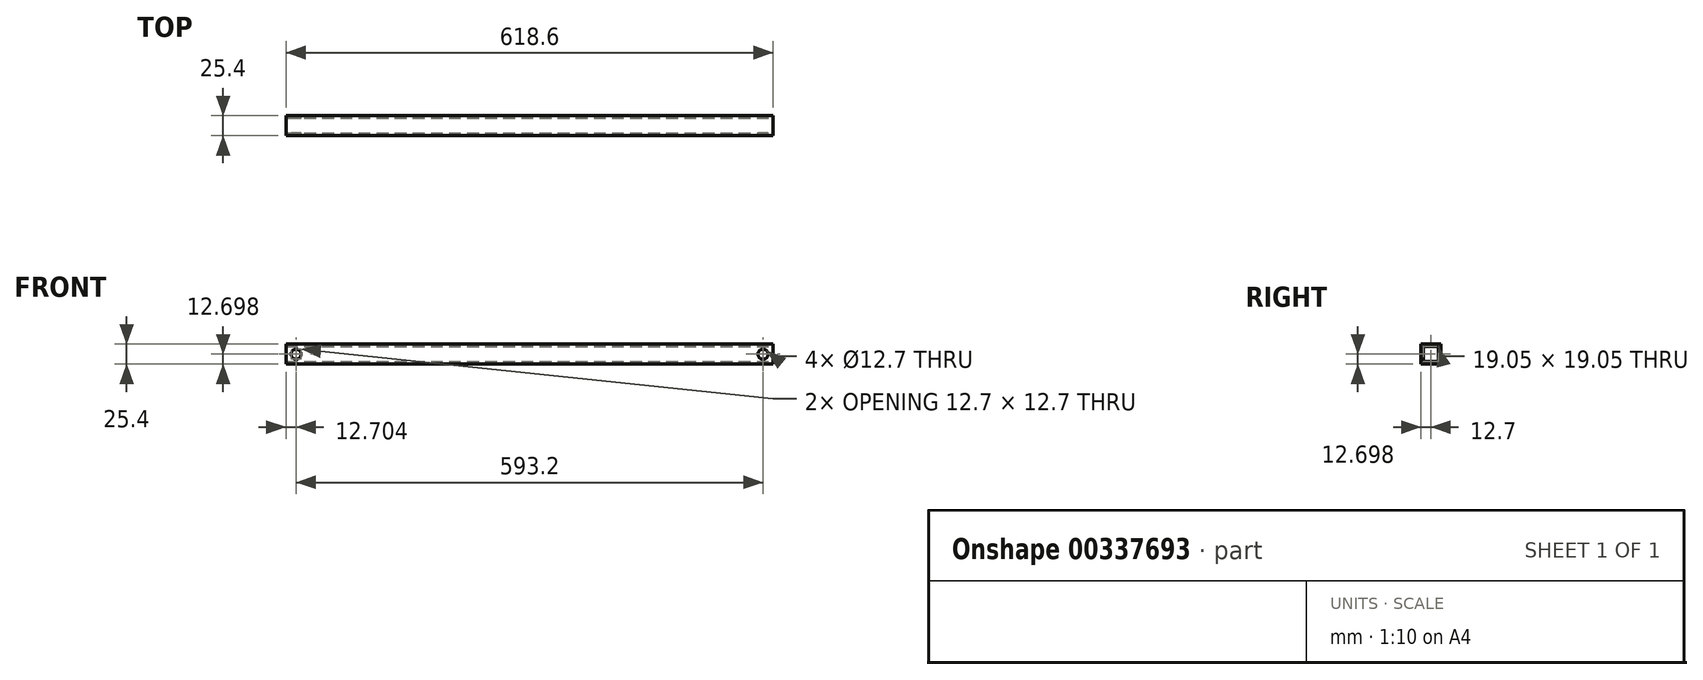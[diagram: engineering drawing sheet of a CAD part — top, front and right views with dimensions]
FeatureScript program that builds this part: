
annotation { "Feature Type Name" : "Feature", "Feature Type Description" : "" }
export const myFeature = defineFeature(function(context is Context, id is Id, definition is map)
    precondition{}
    {
        {
            var Q0;
            Q0=qCreatedBy(makeId("Front.planeOp"),FACE);
            var sketch = newSketch(context, id + "F0", { "sketchPlane" : qUnion([Q0])});
            skLineSegment(sketch, "E0.bottom", {"start": v(-291.49, -54.8) * mm, "end": v(301.71, -54.8) * mm});
            skLineSegment(sketch, "E0.top", {"start": v(-291.49, -80.2) * mm, "end": v(301.71, -80.2) * mm});
            skCircle(sketch, "E1", {"center": v(-291.49, -67.5) * mm, "radius": 6.35 * mm});
            skCircle(sketch, "E2", {"center": v(301.71, -67.5) * mm, "radius": 6.35 * mm});
            skLineSegment(sketch, "E3.bottom", {"start": v(-291.49, -54.8) * mm, "end": v(-304.19, -54.8) * mm});
            skLineSegment(sketch, "E3.top", {"start": v(-291.49, -80.2) * mm, "end": v(-304.19, -80.2) * mm});
            skLineSegment(sketch, "E3.right", {"start": v(-304.19, -54.8) * mm, "end": v(-304.19, -80.2) * mm});
            skLineSegment(sketch, "E4.bottom", {"start": v(301.71, -80.2) * mm, "end": v(314.41, -80.2) * mm});
            skLineSegment(sketch, "E4.top", {"start": v(301.71, -54.8) * mm, "end": v(314.41, -54.8) * mm});
            skLineSegment(sketch, "E4.right", {"start": v(314.41, -80.2) * mm, "end": v(314.41, -54.8) * mm});
            skSolve(sketch);
        }
        {
            var Q0;
            Q0 = qSketchRegion(id + "F0", true);
            extrude(context, id + "F1", {"entities" : qUnion([Q0]), "depth" : 15.88 * mm});
        }
        {
            var Q0;
            Q0 = qSketchRegion(id + "F0", true);
            extrude(context, id + "F2", {"entities" : qUnion([Q0]), "operationType" : NewBodyOperationType.ADD, "depth" : 25.4 * mm});
        }
        {
            var Q0;
            {var subQ0=sQuery(id+"F0.wireOp",EDGE,"E4.right");Q0=makeQuery(id+"F2.boolean.opBoolean","MERGE",FACE,{"derivedFrom":[makeQuery(id+"F1.opExtrude","SWEPT_FACE",FACE,{"disambiguationData":[OSD([subQ0])]}),makeQuery(id+"F2.opExtrude","SWEPT_FACE",FACE,{"disambiguationData":[OSD([subQ0])]})]});}
            var sketch = newSketch(context, id + "F3", { "sketchPlane" : qUnion([Q0])});
            skLineSegment(sketch, "E5.bottom", {"start": v(-22.22, -77.03) * mm, "end": v(-3.17, -77.03) * mm});
            skLineSegment(sketch, "E5.top", {"start": v(-22.23, -57.98) * mm, "end": v(-3.18, -57.98) * mm});
            skLineSegment(sketch, "E5.left", {"start": v(-22.23, -77.03) * mm, "end": v(-22.23, -57.98) * mm});
            skLineSegment(sketch, "E5.right", {"start": v(-3.17, -77.03) * mm, "end": v(-3.18, -57.98) * mm});
            skSolve(sketch);
        }
        {
            var Q0;
            Q0 = qSketchRegion(id + "F3", true);
            extrude(context, id + "F4", {"entities" : qUnion([Q0]), "operationType" : NewBodyOperationType.REMOVE, "endBound" : BoundingType.THROUGH_ALL, "oppositeDirection" : true, "depth" : 25.4 * mm});
        }
    });
